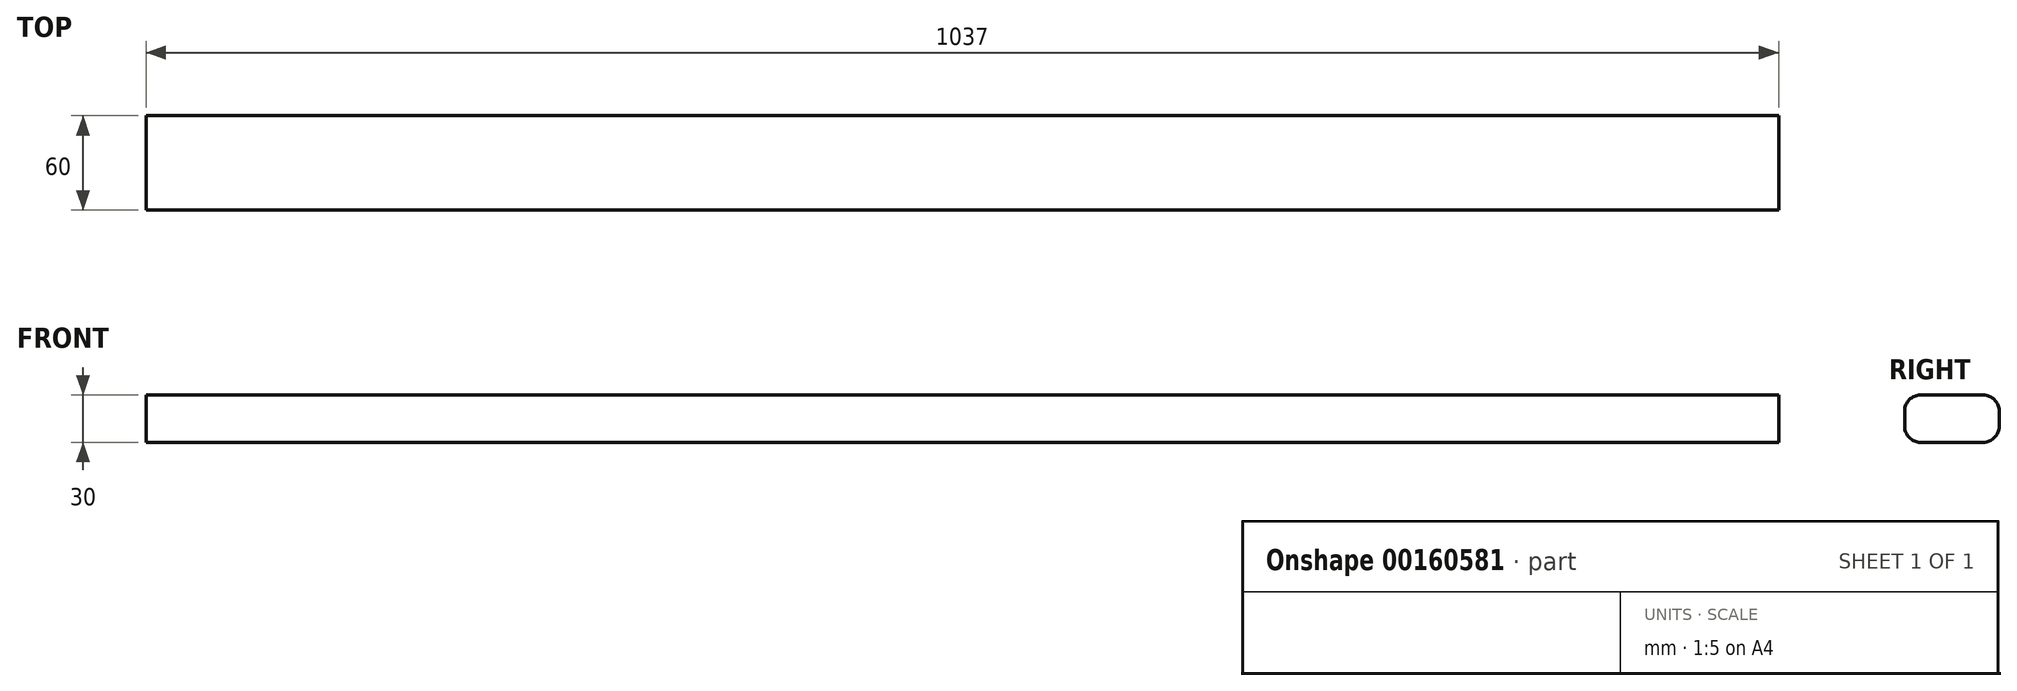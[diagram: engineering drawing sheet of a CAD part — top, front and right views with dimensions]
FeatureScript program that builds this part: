
annotation { "Feature Type Name" : "Feature", "Feature Type Description" : "" }
export const myFeature = defineFeature(function(context is Context, id is Id, definition is map)
    precondition{}
    {
        {
            var Q0;
            Q0=qCreatedBy(makeId("Top.planeOp"),FACE);
            var sketch = newSketch(context, id + "F0", { "sketchPlane" : qUnion([Q0])});
            skLineSegment(sketch, "E0.bottom", {"start": v(-316.52, 30.22) * mm, "end": v(720.48, 30.22) * mm});
            skLineSegment(sketch, "E0.top", {"start": v(-316.52, -29.78) * mm, "end": v(720.48, -29.78) * mm});
            skLineSegment(sketch, "E0.left", {"start": v(-316.52, 30.22) * mm, "end": v(-316.52, -29.78) * mm});
            skLineSegment(sketch, "E0.right", {"start": v(720.48, 30.22) * mm, "end": v(720.48, -29.78) * mm});
            skSolve(sketch);
        }
        {
            var Q0;
            Q0=makeQuery(id+"F0.imprint","IMPRINT",FACE,{"disambiguationData":[TD([[makeQuery(id+"F0.imprint","IMPRINT",EDGE,{"derivedFrom":sQuery(id+"F0.wireOp",EDGE,"E0.bottom")}),-1.0]])]});
            extrude(context, id + "F1", {"entities" : qUnion([Q0]), "depth" : 30 * mm});
        }
        {
            var Q0;
            Q0=makeQuery(id+"F1.opExtrude","CAP_EDGE",EDGE,{"disambiguationData":[OSD([sQuery(id+"F0.wireOp",EDGE,"E0.bottom")])],"isStart":false});
            var Q1;
            Q1=makeQuery(id+"F1.opExtrude","CAP_EDGE",EDGE,{"disambiguationData":[OSD([sQuery(id+"F0.wireOp",EDGE,"E0.bottom")])],"isStart":true});
            var Q2;
            Q2=makeQuery(id+"F1.opExtrude","CAP_EDGE",EDGE,{"disambiguationData":[OSD([sQuery(id+"F0.wireOp",EDGE,"E0.top")])],"isStart":false});
            var Q3;
            Q3=makeQuery(id+"F1.opExtrude","CAP_EDGE",EDGE,{"disambiguationData":[OSD([sQuery(id+"F0.wireOp",EDGE,"E0.top")])],"isStart":true});
            fillet(context, id + "F2", {"entities" : qUnion([Q0, Q1, Q2, Q3]), "radius" : 10 * mm, "tangentPropagation" : true, "allowEdgeOverflow" : false});
        }
    });
